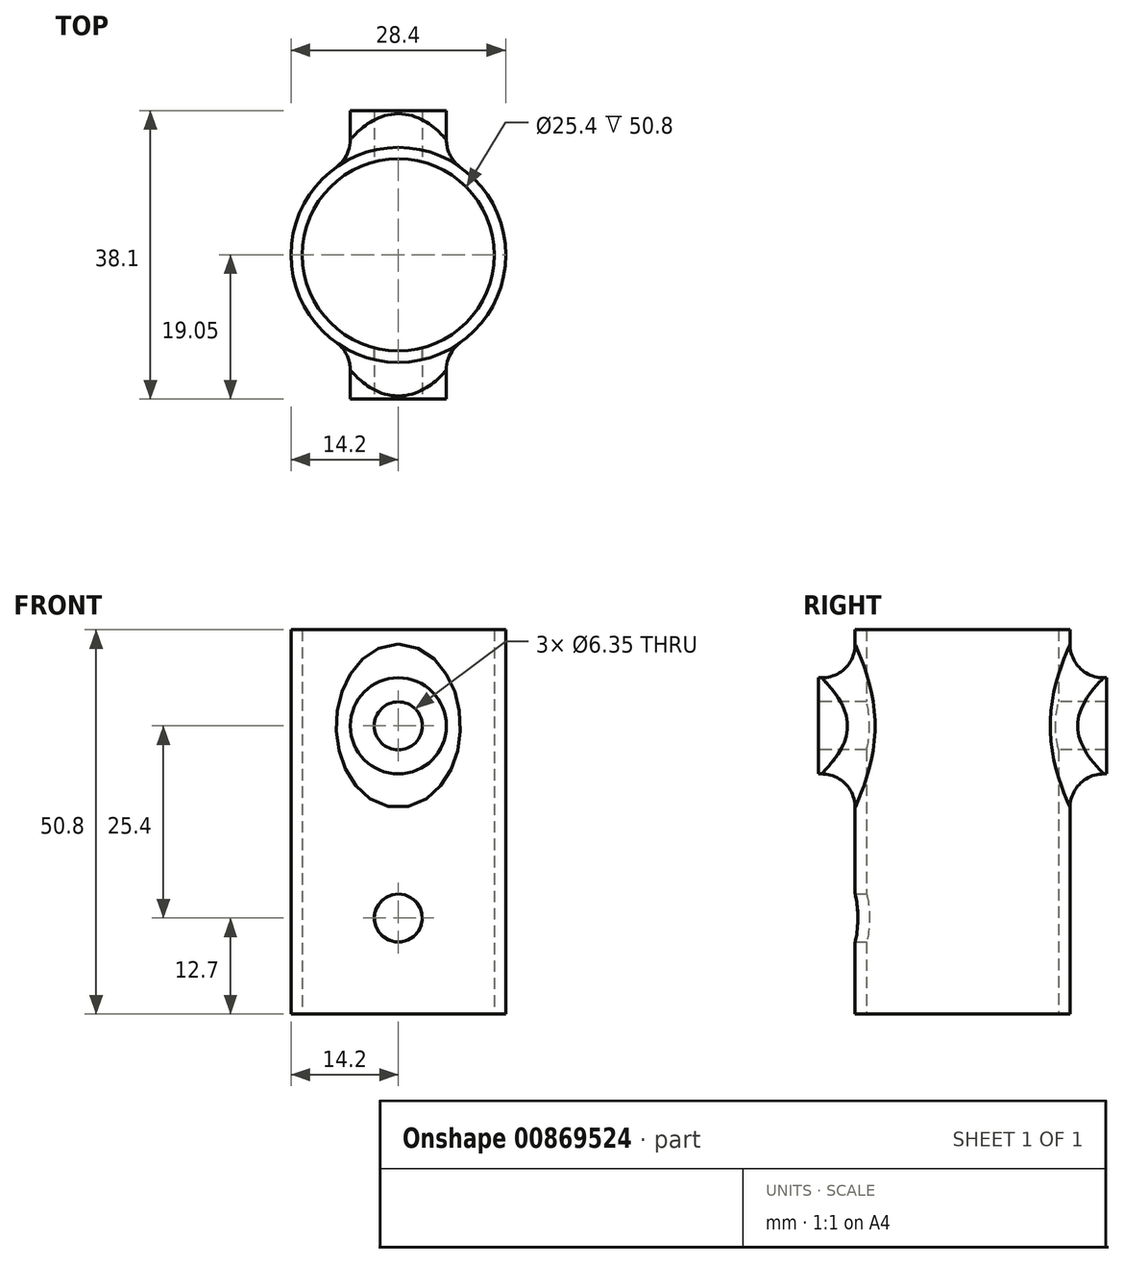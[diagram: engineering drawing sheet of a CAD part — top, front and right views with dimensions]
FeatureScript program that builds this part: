
annotation { "Feature Type Name" : "Feature", "Feature Type Description" : "" }
export const myFeature = defineFeature(function(context is Context, id is Id, definition is map)
    precondition{}
    {
        {
            var Q0;
            Q0=qCreatedBy(makeId("Top.planeOp"),FACE);
            var sketch = newSketch(context, id + "F0", { "sketchPlane" : qUnion([Q0])});
            skCircle(sketch, "E0", {"center": v(0, 0) * mm, "radius": 12.7 * mm, "construction": true});
            skCircle(sketch, "E1.0", {"center": v(0, 0) * mm, "radius": 14.2 * mm});
            skSolve(sketch);
        }
        {
            var Q0;
            Q0 = qSketchRegion(id + "F0", true);
            extrude(context, id + "F1", {"entities" : qUnion([Q0]), "depth" : 50.8 * mm, "offsetDistance" : 25.4 * mm});
        }
        {
            var Q0;
            Q0=qCreatedBy(makeId("Front.planeOp"),FACE);
            var sketch = newSketch(context, id + "F2", { "sketchPlane" : qUnion([Q0])});
            skCircle(sketch, "E2", {"center": v(0, 38.1) * mm, "radius": 6.35 * mm});
            skSolve(sketch);
        }
        {
            var Q0;
            Q0 = qSketchRegion(id + "F2", true);
            extrude(context, id + "F3", {"entities" : qUnion([Q0]), "operationType" : NewBodyOperationType.ADD, "endBound" : BoundingType.SYMMETRIC, "depth" : 38.1 * mm, "offsetDistance" : 25.4 * mm});
        }
        {
            var Q0;
            Q0=sQuery(id+"F0.wireOp",VERTEX,"E0.center");
            var Q1;
            Q1=makeQuery(id+"F1.opExtrude","SWEPT_BODY",BODY,{"disambiguationData":[OSD([sQuery(id+"F0.wireOp",EDGE,"E1.0")])]});
            hole(context, id + "F4", {"style" : HoleStyle.SIMPLE, "endStyle" : HoleEndStyle.BLIND, "oppositeDirection" : true, "holeDiameter" : 25.4 * mm, "majorDiameter" : 6.35 * mm, "holeDepth" : 50.8 * mm, "isTappedThrough" : true, "tappedDepth" : 12.7 * mm, "tapClearance" : 3, "locations" : qUnion([Q0]), "scope" : qUnion([Q1])});
        }
        {
            var Q0;
            Q0=makeQuery(id+"F3.opExtrude","CAP_FACE",FACE,{"disambiguationData":[OSD([sQuery(id+"F2.wireOp",EDGE,"E2")])],"isStart":false});
            cPlane(context, id + "F5", {"entities" : qUnion([Q0]), "cplaneType" : CPlaneType.OFFSET, "offset" : 0 * mm, "width" : 152.4 * mm, "height" : 152.4 * mm});
        }
        {
            var Q0;
            Q0=qCreatedBy(id+"F5.planeOp",FACE);
            var sketch = newSketch(context, id + "F6", { "sketchPlane" : qUnion([Q0])});
            skPoint(sketch, "E3", {"position": v(0, 38.1) * mm});
            skSolve(sketch);
        }
        {
            var Q0;
            Q0=sQuery(id+"F6.wireOp",VERTEX,"E3");
            var Q1;
            Q1=makeQuery(id+"F1.opExtrude","SWEPT_BODY",BODY,{"disambiguationData":[OSD([sQuery(id+"F0.wireOp",EDGE,"E1.0")])]});
            hole(context, id + "F7", {"style" : HoleStyle.SIMPLE, "endStyle" : HoleEndStyle.THROUGH, "holeDiameter" : 6.35 * mm, "majorDiameter" : 6.35 * mm, "isTappedThrough" : true, "tappedDepth" : 12.7 * mm, "tapClearance" : 3, "locations" : qUnion([Q0]), "scope" : qUnion([Q1])});
        }
        {
            var Q0;
            Q0=makeQuery(id+"F3.boolean.opBoolean","INTERSECT",EDGE,{"disambiguationData":[OD(0.0)],"derivedFrom":[makeQuery(id+"F1.opExtrude","SWEPT_FACE",FACE,{"disambiguationData":[OSD([sQuery(id+"F0.wireOp",EDGE,"E1.0")])]}),makeQuery(id+"F3.opExtrude","SWEPT_FACE",FACE,{"disambiguationData":[OSD([sQuery(id+"F2.wireOp",EDGE,"E2")])]})]});
            fillet(context, id + "F8", {"entities" : qUnion([Q0]), "radius" : 4.44 * mm, "tangentPropagation" : true, "allowEdgeOverflow" : false});
        }
        {
            var Q0;
            Q0=makeQuery(id+"F3.boolean.opBoolean","INTERSECT",EDGE,{"disambiguationData":[OD(1.0)],"derivedFrom":[makeQuery(id+"F1.opExtrude","SWEPT_FACE",FACE,{"disambiguationData":[OSD([sQuery(id+"F0.wireOp",EDGE,"E1.0")])]}),makeQuery(id+"F3.opExtrude","SWEPT_FACE",FACE,{"disambiguationData":[OSD([sQuery(id+"F2.wireOp",EDGE,"E2")])]})]});
            fillet(context, id + "F9", {"entities" : qUnion([Q0]), "radius" : 4.44 * mm, "tangentPropagation" : true, "allowEdgeOverflow" : false});
        }
        {
            var Q0;
            Q0=qCreatedBy(makeId("Front.planeOp"),FACE);
            var sketch = newSketch(context, id + "F10", { "sketchPlane" : qUnion([Q0])});
            skCircle(sketch, "E4", {"center": v(0, 12.7) * mm, "radius": 3.18 * mm});
            skSolve(sketch);
        }
        {
            var Q0;
            Q0 = qSketchRegion(id + "F10", true);
            extrude(context, id + "F11", {"entities" : qUnion([Q0]), "operationType" : NewBodyOperationType.REMOVE, "depth" : 25.4 * mm, "offsetDistance" : 25.4 * mm});
        }
    });
